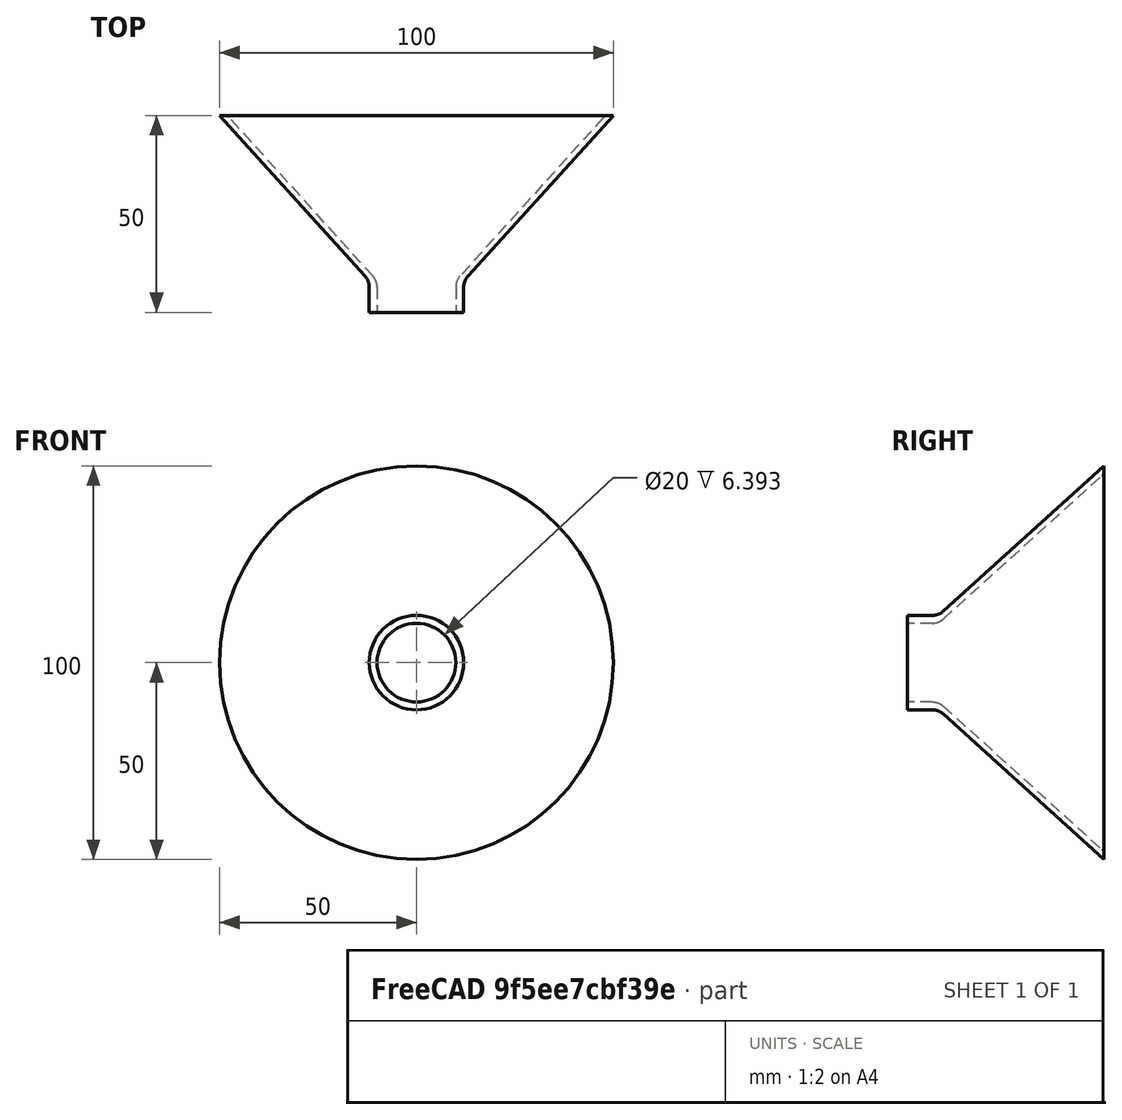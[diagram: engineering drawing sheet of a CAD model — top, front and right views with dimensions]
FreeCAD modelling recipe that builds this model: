
FCSTD DOCUMENT  (FreeCAD 0.22R38261 (Git))
Label: воронка
License: All rights reserved
LicenseURL: https://en.wikipedia.org/wiki/All_rights_reserved
objects: Sketcher::SketchObject×1, PartDesign::Revolution×1, PartDesign::Body×1
note: 5 computed .brp shape members not serialized (recipe doc carries the construction recipe); baked Part::Feature solids carry a one-line shape summary decoded from their .brp

FEATURE [Sketcher::SketchObject] Sketch
  AttachmentSupport = -> [XY_Plane]
  FullyConstrained = false
  MapMode = 5
  sketch-geometry (13):
    g0: LineSegment StartX=10 StartY=-9e-16 StartZ=0 EndX=12 EndY=-9e-16 EndZ=0
    g1: LineSegment StartX=12 StartY=-9e-16 StartZ=0 EndX=12 EndY=6.4038 EndZ=0
    g2: LineSegment StartX=13.0709 StartY=9.18364 StartZ=0 EndX=50 EndY=50 EndZ=0
    g3: LineSegment StartX=50 StartY=50 StartZ=0 EndX=48.7309 EndY=50 EndZ=0
    g4: LineSegment StartX=47.5096 StartY=49.458 StartZ=0 EndX=11.0783 EndY=9.19186 EndZ=0
    g5: LineSegment StartX=10 StartY=6.39271 StartZ=0 EndX=10 EndY=-9e-16 EndZ=0
    g6: GeomPoint X=0 Y=50 Z=0
    g7: ArcOfCircle CenterX=14.1721 CenterY=6.39271 CenterZ=0 NormalX=0 NormalY=0 NormalZ=1 AngleXU=0 Radius=4.17214 StartAngle=2.40615 EndAngle=3.14159
    g8: GeomPoint X=10 Y=8 Z=0
    g9: ArcOfCircle CenterX=16.1434 CenterY=6.4038 CenterZ=0 NormalX=0 NormalY=0 NormalZ=1 AngleXU=0 Radius=4.14337 StartAngle=2.40615 EndAngle=3.14159
    g10: GeomPoint X=12 Y=8 Z=0
    g11: ArcOfCircle CenterX=48.7309 CenterY=48.3531 CenterZ=0 NormalX=0 NormalY=0 NormalZ=1 AngleXU=0 Radius=1.64689 StartAngle=1.5708 EndAngle=2.40615
    g12: GeomPoint X=48 Y=50 Z=0
  constraints (28):
    c: Coincident(g1,g0)
    c: Vertical(g1)
    c: Vertical(g5)
    c: Horizontal(g3)
    c: Coincident(g2,g3)
    c: Distance(g3,g12) = 2
    c: Horizontal(g10,g8)
    c: Coincident(g0,g5)
    c: Distance(g5,g8) = 8
    c: Horizontal(g0)
    c: Distance(g0) = 2
    c: Distance(g-1,g0) = 12
    c: PointOnObject(g6,g-2)
    c: Distance(g-1,g6) = 50
    c: Horizontal(g6,g12)
    c: Distance(g6,g2) = 50
    c: PointOnObject(g8,g5)
    c: PointOnObject(g8,g4)
    c: Tangent(g5,g7) = -1.5708
    c: Tangent(g4,g7) = -1.5708
    c: PointOnObject(g10,g1)
    c: PointOnObject(g10,g2)
    c: Tangent(g1,g9) = 1.5708
    c: Tangent(g2,g9) = 1.5708
    c: PointOnObject(g12,g4)
    c: PointOnObject(g12,g3)
    c: Tangent(g4,g11) = -1.5708
    c: Tangent(g3,g11) = -1.5708
FEATURE [PartDesign::Revolution] Revolution
  Angle = 360
  Angle2 = 60
  Axis = (0,1,0)
  Base = (0,0,0)
  Profile = -> Sketch
  ReferenceAxis = -> Sketch [V_Axis]
  Reversed = true
  Suppressed = false
  Type = 0
FEATURE [PartDesign::Body] Body  label="Тело"
  AllowCompound = false
  Group = -> [Sketch,Revolution]
  Origin = -> Origin
  Tip = -> Revolution
